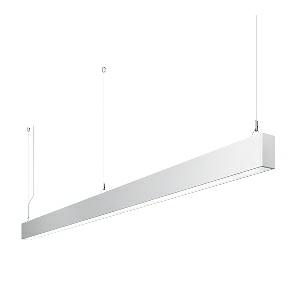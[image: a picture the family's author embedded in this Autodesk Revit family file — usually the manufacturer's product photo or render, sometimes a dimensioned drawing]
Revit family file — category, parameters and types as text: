
# Revit family: idoo_line_-_ilp_6000_840_d_00805677_cd12
name_source: partatom
category: Lighting Fixtures
units: mm (PartAtom-declared; Revit-internal decimal feet)

## family parameters
Cut with Voids When Loaded = No
Host = Face
Light Source = No
Part Type = Normal
Room Calculation Point = No
Round Connector Dimension = Use Diameter
Shared = No

## types (1)
- IDOO.line - ILP 6000/840/D (1 x LED, 6300 lm, 4000K)
    Apparent Load = 46 VA
    Approval mark = CE
    CIE Flux Codes = 66 91 98 40 100
    Color Rendering = 80-89
    Color Temperature = 4000K
    Control Gear = Electronic ballast
    Default Elevation = 1800 mm
    Description = ILP 6000/840/D|Suspended luminaire|light source: LED|connected load: 220-240V, 50/60Hz|Power consumption: approx. 46 W|standby: approx. 0,15|luminous flux: 6300 lm|luminous efficacy: 136 lm/W|light distribution: Direct/indirect|direct ratio: approx. 40 %|colour temperature: Cold white, ca. 4000 K|color rendering index (CRI): >= 80|chromaticity tolerance:  3 SDCM|System of protection: IP 40|technology: Continuously dimmable|luminaire body|material: Sectional aluminium|colour: White|lamp cover: Acrylic (PMMA), Clear|mains lead: 2.00 m With free stranded wires|Fastening: Steel cable 0.3 - 0.7 m|glare control: Prism aperture|luminance(L65): <= 2700 cd/m|unified glare rating(4H 8H): <=  16|special features: DALI Load 1x, TouchDIM - dimming via standard switch, Flicker-free, Suitable as emergency lighting|
    Frequency = 50 Hz
    Height = 110 mm
    Lamp = 1 x LED
    Lamp Light Flux = 6300 lm
    Lamp count = 1
    Length = 2256 mm
    Luminous efficacy = 137 lm/W
    Manufacturer = Waldmann
    ModVariant = No
    Model = 00805677
    Mounting Place = Ceiling
    Mounting Type = Pendant
    Number of Poles = 1
    OnlyDefault = Yes
    Power Factor = 1
    Product Name = IDOO.line - ILP 6000/840/D
    Product group = Suspended luminaire
    ProductGroupID = 9
    Protection Class = Protection class I
    Protection Degree = IP 40
    RLX_Detail_Level = 1
    RLX_Emergency_Light_Flux = 0 lm
    RLX_Emergency_Type = 0
    RLX_Emergency_Type_DB = No
    RlxData = <blob elided: 21165 chars, md5=1f87a6ac>
    Socket = socket
    Standby Power = 0 W
    System Light Flux = 6300 lm
    System Power = 46 W
    Type Comments = Product without accessories
    Type Image = 113293000-00692530.jpg
    URL = http://relux.com
    VarID = ---
    Voltage = 230 V
    Voltage Range = 220-240 V
    Weight = 0.00 kg
    Width = 60 mm  [stored 0.19685 ft]

note: [stored X ft] marks values corroborated as IEEE doubles in the binary element streams (Revit-internal decimal feet)

## geometry (parser evidence)
native form markers: Blend x4, Sweep x14
no freeform markers — native parametric forms only
